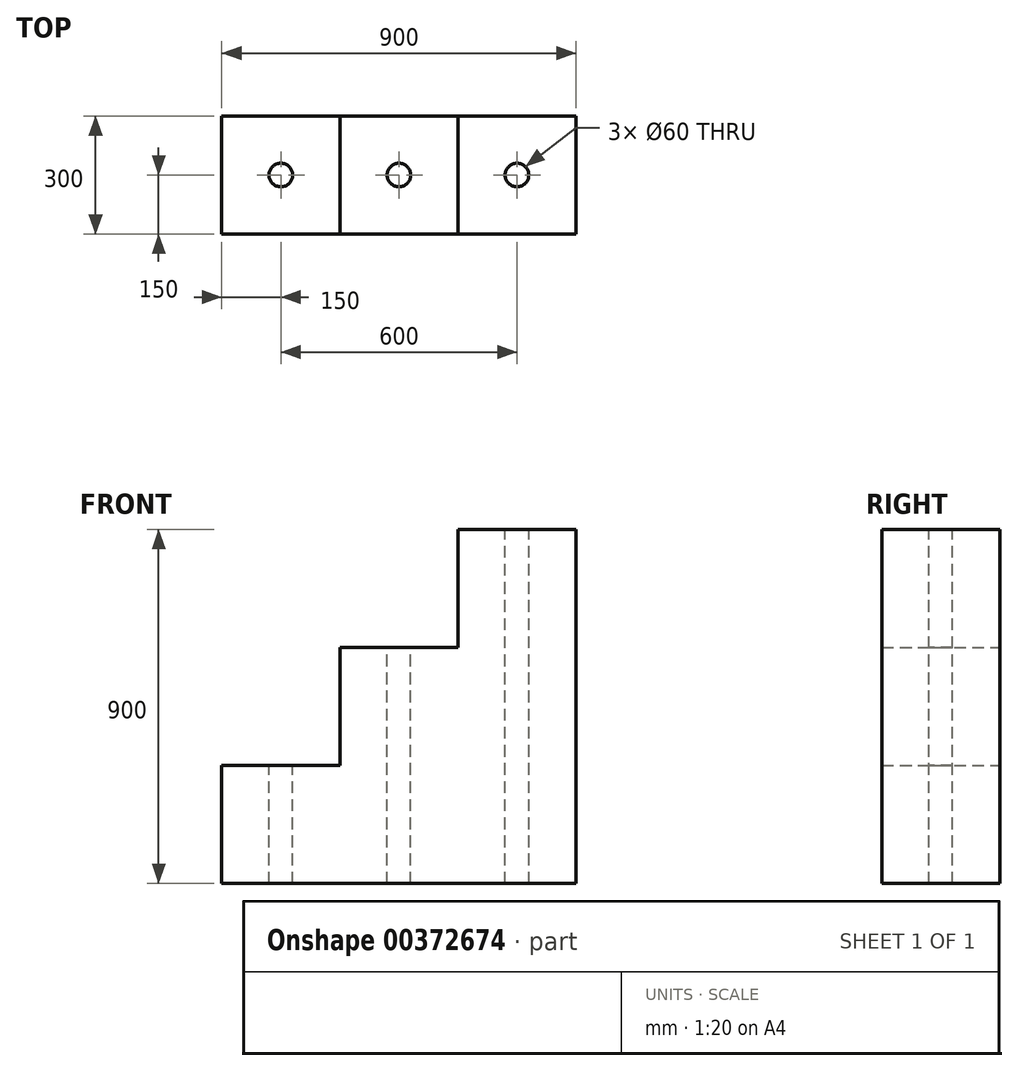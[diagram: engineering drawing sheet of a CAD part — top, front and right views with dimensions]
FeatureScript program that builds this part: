
annotation { "Feature Type Name" : "Feature", "Feature Type Description" : "" }
export const myFeature = defineFeature(function(context is Context, id is Id, definition is map)
    precondition{}
    {
        {
            var Q0;
            Q0=qCreatedBy(makeId("Front.planeOp"),FACE);
            var sketch = newSketch(context, id + "F0", { "sketchPlane" : qUnion([Q0])});
            skLineSegment(sketch, "E0", {"start": v(0, 0) * mm, "end": v(900, 0) * mm});
            skLineSegment(sketch, "E1", {"start": v(900, 0) * mm, "end": v(900, 900) * mm});
            skLineSegment(sketch, "E2", {"start": v(900, 900) * mm, "end": v(600, 900) * mm});
            skLineSegment(sketch, "E3", {"start": v(600, 900) * mm, "end": v(600, 600) * mm});
            skLineSegment(sketch, "E4", {"start": v(600, 600) * mm, "end": v(300, 600) * mm});
            skLineSegment(sketch, "E5", {"start": v(300, 600) * mm, "end": v(300, 300) * mm});
            skLineSegment(sketch, "E6", {"start": v(300, 300) * mm, "end": v(0, 300) * mm});
            skLineSegment(sketch, "E7", {"start": v(0, 300) * mm, "end": v(0, 0) * mm});
            skSolve(sketch);
        }
        {
            var Q0;
            Q0=makeQuery(id+"F0.imprint","IMPRINT",FACE,{"disambiguationData":[TD([[makeQuery(id+"F0.imprint","IMPRINT",EDGE,{"derivedFrom":sQuery(id+"F0.wireOp",EDGE,"E0")}),1.0]])]});
            extrude(context, id + "F1", {"entities" : qUnion([Q0]), "depth" : 300 * mm});
        }
        {
            var Q0;
            Q0=makeQuery(id+"F1.opExtrude","SWEPT_FACE",FACE,{"disambiguationData":[OSD([sQuery(id+"F0.wireOp",EDGE,"E2")])]});
            var sketch = newSketch(context, id + "F2", { "sketchPlane" : qUnion([Q0])});
            skCircle(sketch, "E8", {"center": v(750, -150) * mm, "radius": 10 * mm});
            skPoint(sketch, "E8.centerSnap0", {"position": v(900, -150) * mm});
            skPoint(sketch, "E8.centerSnap1", {"position": v(750, 0) * mm});
            skSolve(sketch);
        }
        {
            var Q0;
            Q0=sQuery(id+"F2.wireOp",VERTEX,"E8.center");
            var Q1;
            Q1=makeQuery(id+"F1.opExtrude","SWEPT_BODY",BODY,{"disambiguationData":[OSD([sQuery(id+"F0.wireOp",EDGE,"E0"),sQuery(id+"F0.wireOp",EDGE,"E1"),sQuery(id+"F0.wireOp",EDGE,"E2"),sQuery(id+"F0.wireOp",EDGE,"E3"),sQuery(id+"F0.wireOp",EDGE,"E4"),sQuery(id+"F0.wireOp",EDGE,"E5"),sQuery(id+"F0.wireOp",EDGE,"E6"),sQuery(id+"F0.wireOp",EDGE,"E7")])]});
            hole(context, id + "F3", {"style" : HoleStyle.SIMPLE, "endStyle" : HoleEndStyle.THROUGH, "holeDiameter" : 60 * mm, "isTappedThrough" : true, "tappedDepth" : 12 * mm, "tapClearance" : 3, "locations" : qUnion([Q0]), "scope" : qUnion([Q1])});
        }
        {
            var Q0;
            Q0=makeQuery(id+"F1.opExtrude","SWEPT_FACE",FACE,{"disambiguationData":[OSD([sQuery(id+"F0.wireOp",EDGE,"E4")])]});
            var sketch = newSketch(context, id + "F4", { "sketchPlane" : qUnion([Q0])});
            skCircle(sketch, "E9", {"center": v(450, -150) * mm, "radius": 15 * mm});
            skPoint(sketch, "E9.centerSnap0", {"position": v(600, -150) * mm});
            skPoint(sketch, "E9.centerSnap1", {"position": v(450, 0) * mm});
            skSolve(sketch);
        }
        {
            var Q0;
            Q0=makeQuery(id+"F1.opExtrude","SWEPT_FACE",FACE,{"disambiguationData":[OSD([sQuery(id+"F0.wireOp",EDGE,"E6")])]});
            var sketch = newSketch(context, id + "F5", { "sketchPlane" : qUnion([Q0])});
            skCircle(sketch, "E10", {"center": v(150, -150) * mm, "radius": 15 * mm});
            skPoint(sketch, "E10.centerSnap0", {"position": v(300, -150) * mm});
            skPoint(sketch, "E10.centerSnap1", {"position": v(150, 0) * mm});
            skSolve(sketch);
        }
        {
            var Q0;
            Q0=sQuery(id+"F5.wireOp",VERTEX,"E10.center");
            var Q1;
            Q1=makeQuery(id+"F1.opExtrude","SWEPT_BODY",BODY,{"disambiguationData":[OSD([sQuery(id+"F0.wireOp",EDGE,"E0"),sQuery(id+"F0.wireOp",EDGE,"E1"),sQuery(id+"F0.wireOp",EDGE,"E2"),sQuery(id+"F0.wireOp",EDGE,"E3"),sQuery(id+"F0.wireOp",EDGE,"E4"),sQuery(id+"F0.wireOp",EDGE,"E5"),sQuery(id+"F0.wireOp",EDGE,"E6"),sQuery(id+"F0.wireOp",EDGE,"E7")])]});
            hole(context, id + "F6", {"style" : HoleStyle.SIMPLE, "endStyle" : HoleEndStyle.THROUGH, "holeDiameter" : 60 * mm, "isTappedThrough" : true, "tappedDepth" : 12 * mm, "tapClearance" : 3, "locations" : qUnion([Q0]), "scope" : qUnion([Q1])});
        }
        {
            var Q0;
            Q0=sQuery(id+"F4.wireOp",VERTEX,"E9.center");
            var Q1;
            Q1=makeQuery(id+"F1.opExtrude","SWEPT_BODY",BODY,{"disambiguationData":[OSD([sQuery(id+"F0.wireOp",EDGE,"E0"),sQuery(id+"F0.wireOp",EDGE,"E1"),sQuery(id+"F0.wireOp",EDGE,"E2"),sQuery(id+"F0.wireOp",EDGE,"E3"),sQuery(id+"F0.wireOp",EDGE,"E4"),sQuery(id+"F0.wireOp",EDGE,"E5"),sQuery(id+"F0.wireOp",EDGE,"E6"),sQuery(id+"F0.wireOp",EDGE,"E7")])]});
            hole(context, id + "F7", {"style" : HoleStyle.SIMPLE, "endStyle" : HoleEndStyle.THROUGH, "holeDiameter" : 60 * mm, "isTappedThrough" : true, "tappedDepth" : 12 * mm, "tapClearance" : 3, "locations" : qUnion([Q0]), "scope" : qUnion([Q1])});
        }
    });
